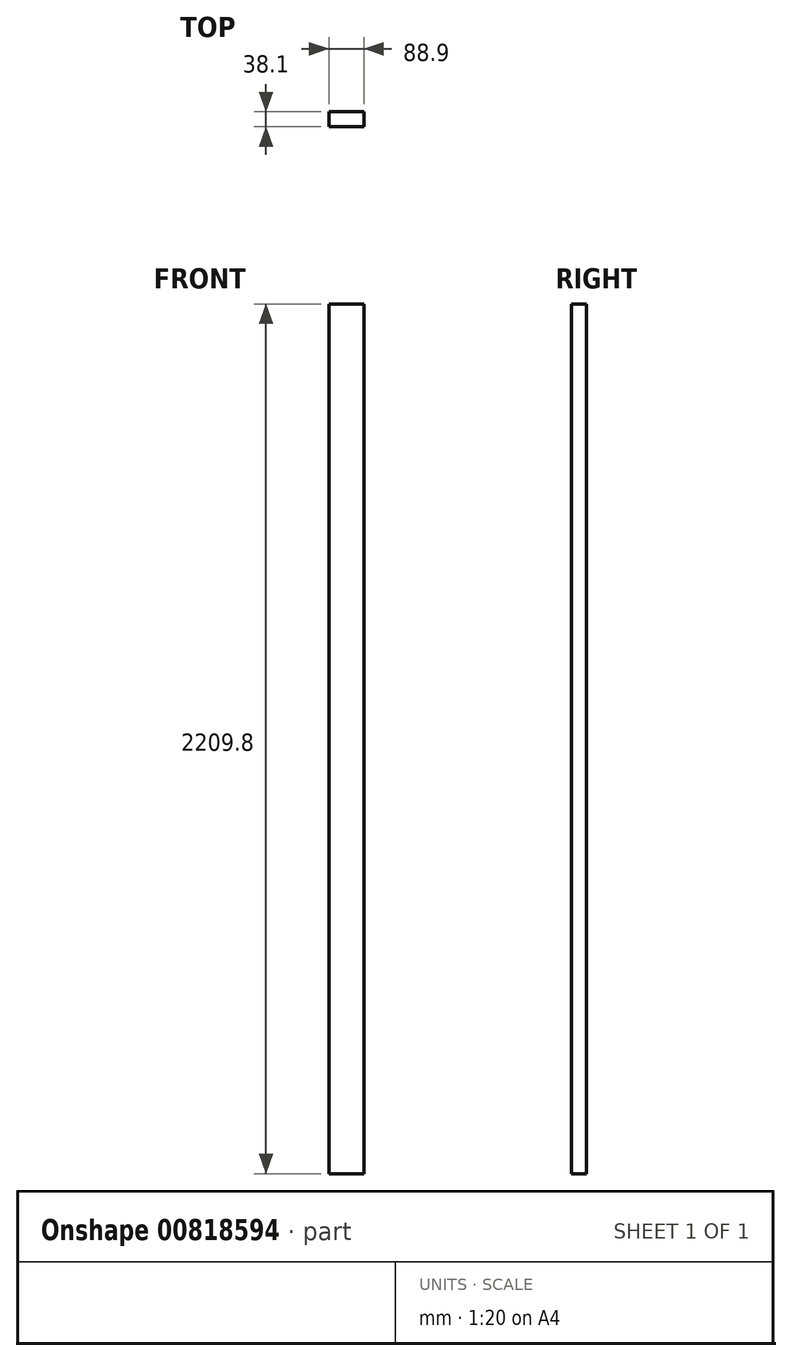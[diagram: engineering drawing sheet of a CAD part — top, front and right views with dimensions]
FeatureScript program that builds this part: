
annotation { "Feature Type Name" : "Feature", "Feature Type Description" : "" }
export const myFeature = defineFeature(function(context is Context, id is Id, definition is map)
    precondition{}
    {
        {
            var Q0;
            Q0=qCreatedBy(makeId("Front.planeOp"),FACE);
            var sketch = newSketch(context, id + "F0", { "sketchPlane" : qUnion([Q0])});
            skLineSegment(sketch, "E0.bottom", {"start": v(0, 0) * mm, "end": v(88.9, 0) * mm});
            skLineSegment(sketch, "E0.top", {"start": v(0, 2209.8) * mm, "end": v(88.9, 2209.8) * mm});
            skLineSegment(sketch, "E0.left", {"start": v(0, 0) * mm, "end": v(0, 2209.8) * mm});
            skLineSegment(sketch, "E0.right", {"start": v(88.9, 0) * mm, "end": v(88.9, 2209.8) * mm});
            skSolve(sketch);
        }
        {
            var Q0;
            Q0 = qSketchRegion(id + "F0", true);
            extrude(context, id + "F1", {"entities" : qUnion([Q0]), "depth" : 38.1 * mm, "offsetDistance" : 25.4 * mm});
        }
    });
